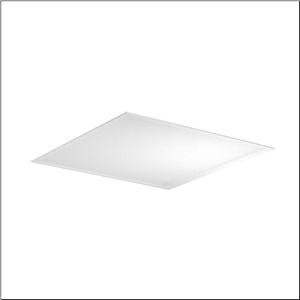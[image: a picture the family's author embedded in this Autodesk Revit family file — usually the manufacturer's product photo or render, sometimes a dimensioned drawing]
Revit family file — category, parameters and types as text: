
# Revit family: apollon_r__31_square_51mp12w72m42_8acd
name_source: partatom
category: Lighting Fixtures
units: mm (PartAtom-declared; Revit-internal decimal feet)

## family parameters
Cut with Voids When Loaded = No
Host = Face
Light Source = No
Part Type = Normal
Room Calculation Point = No
Round Connector Dimension = Use Diameter
Shared = No

## types (1)
- --- (1 x LED, 4000 lm, 27.5 W, 4000K)
    Apparent Load = 28 VA
    CIE Flux Codes = 62 87 97 100 100
    Color Rendering = 80
    Color Temperature = 4000K
    Default Elevation = 1800 mm
    Description = Apollon® 31 square, office luminaire, primary optical cover: micro prismatic cover, of PMMA, CAT 2 (L<= 3000cd/m²), light emission: direct distribution, primary light characteristic: symmetric, installation type: lay-in mounting, LED, rated luminous flux: 4.000lm, luminous efficacy: 145lm/W, light colour: 830/840, colour temperature: 3000/4000K, with terminal, 3-pole, mains connection: 220..240V, AC, 50/60Hz, rated input power: 28W, housing, of aluminium, traffic white (RAL 9016), module: M600, length: 595mm, width: 595mm, height: 32mm, housing upper side, of sheet steel, galvanised, protection rating (complete): IP20, protection rating (on room side): IP40, insulation class (complete): insulation class II (safety insulation), certification: CE, ENEC, impact resistance: IK03, permissible operating ambient temperature: -20..+40°C, permissible storage temperature: -20..+60°C, packaging unit: 1 piece
    Height = 0 mm  [stored 0 ft]
    Lamp = 1 x LED
    Lamp Light Flux = 4000 lm
    Lamp Power = 27.5 W
    Lamp count = 1
    Length = 595 mm
    Luminous efficacy = 145 lm/W
    Manufacturer = Siteco
    ModVariant = No
    Model = 51MP12W72M42
    Mounting Place = Ceiling
    Mounting Type = Recessed
    Number of Poles = 1
    OnlyDefault = Yes
    Power Factor = 1
    Product Name = Apollon® 31 square
    Product group = office luminaire | ceiling recessed
    ProductGroupID = 401
    Protection Class = Protection class II
    Protection Degree = IP 20
    RLX_Detail_Level = 1
    RLX_Emergency_Light_Flux = 0 lm
    RLX_Emergency_Type = 0
    RLX_Emergency_Type_DB = No
    RlxData = <blob elided: 12717 chars, md5=0adc2288>
    Socket = socket
    Standby Power = 0 W
    System Light Flux = 4000 lm
    System Power = 28 W
    Type Comments = factory setting: colour temperature 4000K
    Type Image = l_1291035.jpg
    URL = http://relux.com
    VarID = @adj_027785
    Voltage = 0 V
    Weight = 0.00 kg
    Width = 595 mm

note: [stored X ft] marks values corroborated as IEEE doubles in the binary element streams (Revit-internal decimal feet)

## geometry (parser evidence)
native form markers: Sweep x10
no freeform markers — native parametric forms only
